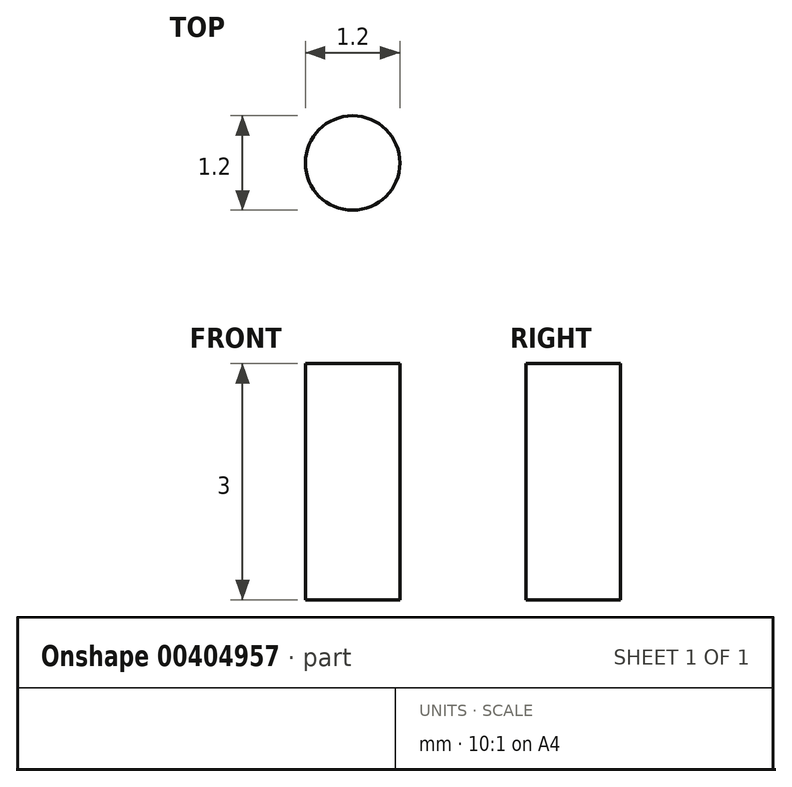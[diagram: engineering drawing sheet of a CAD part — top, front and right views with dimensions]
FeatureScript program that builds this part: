
annotation { "Feature Type Name" : "Feature", "Feature Type Description" : "" }
export const myFeature = defineFeature(function(context is Context, id is Id, definition is map)
    precondition{}
    {
        {
            var Q0;
            Q0=qCreatedBy(makeId("Top.planeOp"),FACE);
            var sketch = newSketch(context, id + "F0", { "sketchPlane" : qUnion([Q0])});
            skCircle(sketch, "E0", {"center": v(0, 0) * mm, "radius": 0.6 * mm});
            skSolve(sketch);
        }
        {
            var Q0;
            Q0=qSketchRegion(id+"F0",true);
            extrude(context, id + "F1", {"entities" : qUnion([Q0]), "depth" : 3 * mm});
        }
    });
